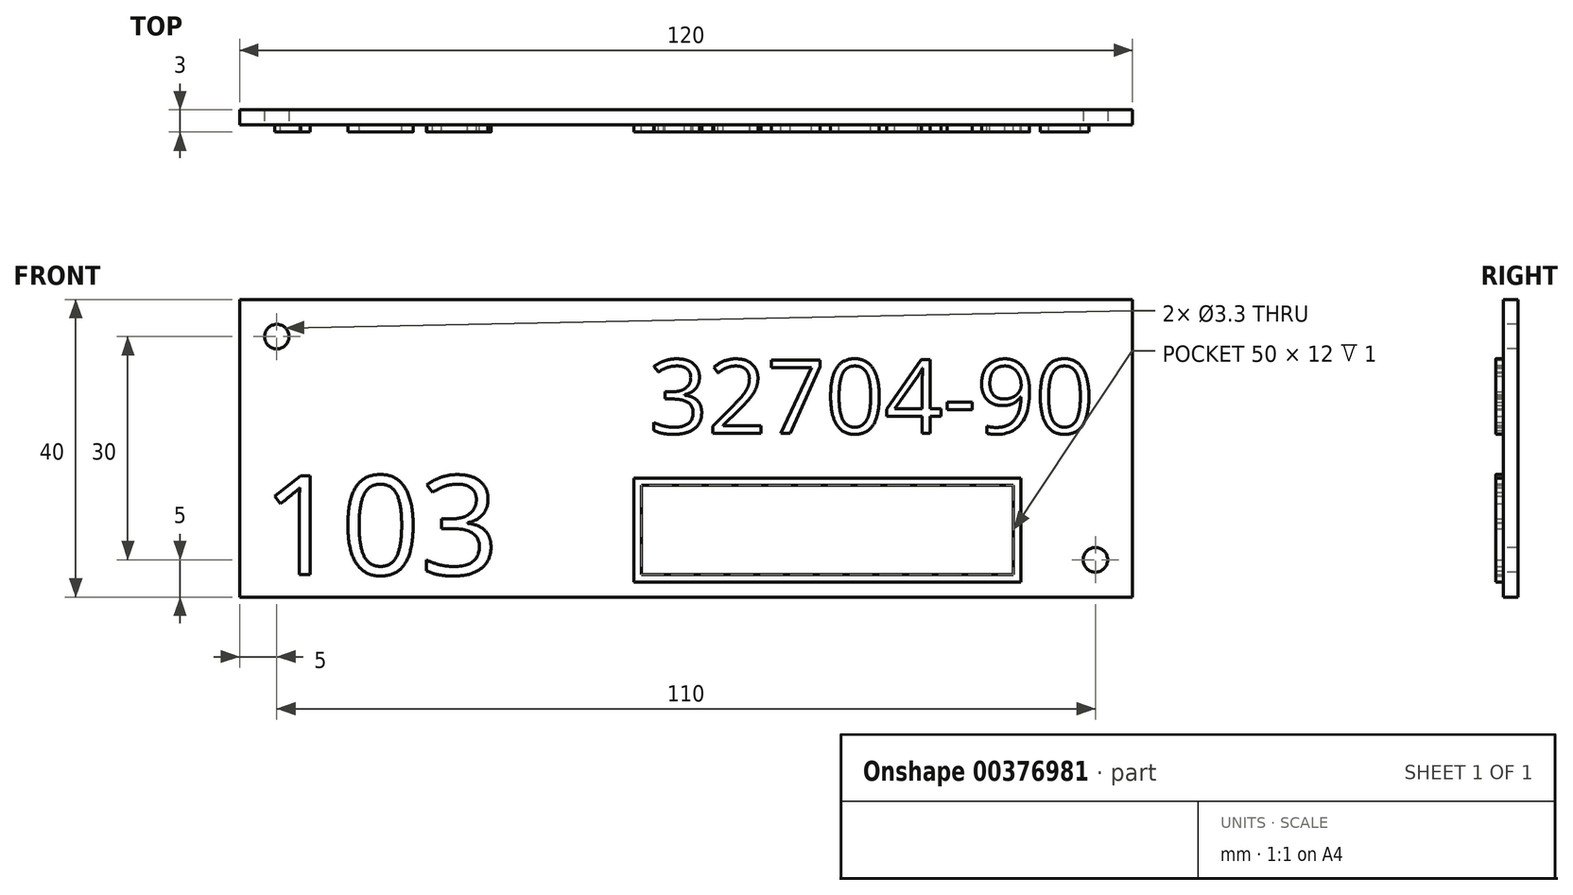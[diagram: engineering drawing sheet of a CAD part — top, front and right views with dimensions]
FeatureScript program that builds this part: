
annotation { "Feature Type Name" : "Feature", "Feature Type Description" : "" }
export const myFeature = defineFeature(function(context is Context, id is Id, definition is map)
    precondition{}
    {
        {
            var Q0;
            Q0=qCreatedBy(makeId("Front.planeOp"),FACE);
            var sketch = newSketch(context, id + "F0", { "sketchPlane" : qUnion([Q0])});
            skLineSegment(sketch, "E0.bottom", {"start": v(60, -20) * mm, "end": v(-60, -20) * mm});
            skLineSegment(sketch, "E0.top", {"start": v(60, 20) * mm, "end": v(-60, 20) * mm});
            skLineSegment(sketch, "E0.left", {"start": v(60, -20) * mm, "end": v(60, 20) * mm});
            skLineSegment(sketch, "E0.right", {"start": v(-60, -20) * mm, "end": v(-60, 20) * mm});
            skPoint(sketch, "E0.middle", {"position": v(0, 0) * mm});
            skSolve(sketch);
        }
        {
            var Q0;
            Q0=makeQuery(id+"F0.imprint","IMPRINT",FACE,{"disambiguationData":[TD([[makeQuery(id+"F0.imprint","IMPRINT",EDGE,{"derivedFrom":sQuery(id+"F0.wireOp",EDGE,"E0.bottom")}),-1.0]])]});
            extrude(context, id + "F1", {"entities" : qUnion([Q0]), "depth" : 2 * mm});
        }
        {
            var Q0;
            Q0=makeQuery(id+"F1.opExtrude","CAP_FACE",FACE,{"disambiguationData":[OSD([sQuery(id+"F0.wireOp",EDGE,"E0.bottom"),sQuery(id+"F0.wireOp",EDGE,"E0.top"),sQuery(id+"F0.wireOp",EDGE,"E0.left"),sQuery(id+"F0.wireOp",EDGE,"E0.right")])],"isStart":false});
            var sketch = newSketch(context, id + "F2", { "sketchPlane" : qUnion([Q0])});
            skPoint(sketch, "E1", {"position": v(-55, 15) * mm});
            skPoint(sketch, "E2", {"position": v(55, -15) * mm});
            skSolve(sketch);
        }
        {
            var Q0;
            Q0=sQuery(id+"F2.wireOp",VERTEX,"E1");
            var Q1;
            Q1=sQuery(id+"F2.wireOp",VERTEX,"E2");
            var Q2;
            Q2=makeQuery(id+"F1.opExtrude","SWEPT_BODY",BODY,{"disambiguationData":[OSD([sQuery(id+"F0.wireOp",EDGE,"E0.bottom"),sQuery(id+"F0.wireOp",EDGE,"E0.top"),sQuery(id+"F0.wireOp",EDGE,"E0.left"),sQuery(id+"F0.wireOp",EDGE,"E0.right")])]});
            hole(context, id + "F3", {"style" : HoleStyle.SIMPLE, "endStyle" : HoleEndStyle.THROUGH, "holeDiameter" : 3.3 * mm, "locations" : qUnion([Q0, Q1]), "scope" : qUnion([Q2]), "isTappedThrough" : true});
        }
        {
            var Q0;
            Q0=makeQuery(id+"F1.opExtrude","CAP_FACE",FACE,{"disambiguationData":[OSD([sQuery(id+"F0.wireOp",EDGE,"E0.bottom"),sQuery(id+"F0.wireOp",EDGE,"E0.top"),sQuery(id+"F0.wireOp",EDGE,"E0.left"),sQuery(id+"F0.wireOp",EDGE,"E0.right")])],"isStart":false});
            var sketch = newSketch(context, id + "F4", { "sketchPlane" : qUnion([Q0])});
            skText(sketch, "E3", { "text": "32704-90", "fontName": "OpenSans-Regular.ttf"});
            const initialGuessF4  = {"E3": [-0.005, 0.002, 1, 0, 0.00996]};
            skSetInitialGuess(sketch, initialGuessF4);
            skSolve(sketch);
        }
        {
            var Q0;
            Q0=qSketchRegion(id+"F4",true);
            extrude(context, id + "F5", {"entities" : qUnion([Q0]), "operationType" : NewBodyOperationType.ADD, "depth" : 1 * mm});
        }
        {
            var Q0;
            {var subQ0=sQuery(id+"F0.wireOp",EDGE,"E0.top");var subQ1=sQuery(id+"F0.wireOp",EDGE,"E0.left");var subQ2=sQuery(id+"F0.wireOp",EDGE,"E0.right");var subQ3=sQuery(id+"F0.wireOp",EDGE,"E0.bottom");Q0=makeQuery(id+"F5.boolean.opBoolean","SPLIT",FACE,{"disambiguationData":[TD([makeQuery(id+"F1.opExtrude","SWEPT_FACE",FACE,{"disambiguationData":[OSD([subQ3])]})])],"derivedFrom":makeQuery(id+"F1.opExtrude","CAP_FACE",FACE,{"disambiguationData":[OSD([subQ3,subQ0,subQ1,subQ2])],"isStart":false})});}
            var sketch = newSketch(context, id + "F6", { "sketchPlane" : qUnion([Q0])});
            skText(sketch, "E4", { "text": "103", "fontName": "OpenSans-Regular.ttf"});
            const initialGuessF6  = {"E4": [-0.057, -0.017, 1, 0, 0.01338]};
            skSetInitialGuess(sketch, initialGuessF6);
            skSolve(sketch);
        }
        {
            var Q0;
            Q0=qSketchRegion(id+"F6",true);
            extrude(context, id + "F7", {"entities" : qUnion([Q0]), "operationType" : NewBodyOperationType.ADD, "depth" : 1 * mm});
        }
        {
            var Q0;
            {var subQ46=sQuery(id+"F0.wireOp",EDGE,"E0.top");var subQ48=sQuery(id+"F0.wireOp",EDGE,"E0.left");var subQ66=sQuery(id+"F0.wireOp",EDGE,"E0.right");var subQ76=sQuery(id+"F0.wireOp",EDGE,"E0.bottom");var subQ77=makeQuery(id+"F1.opExtrude","SWEPT_FACE",FACE,{"disambiguationData":[OSD([subQ76])]});Q0=makeQuery(id+"F7.boolean.opBoolean","SPLIT",FACE,{"disambiguationData":[TD([subQ77])],"derivedFrom":makeQuery(id+"F5.boolean.opBoolean","SPLIT",FACE,{"disambiguationData":[TD([subQ77])],"derivedFrom":makeQuery(id+"F1.opExtrude","CAP_FACE",FACE,{"disambiguationData":[OSD([subQ76,subQ46,subQ48,subQ66])],"isStart":false})})});}
            var sketch = newSketch(context, id + "F8", { "sketchPlane" : qUnion([Q0])});
            skLineSegment(sketch, "E5.bottom", {"start": v(45, -18) * mm, "end": v(-7, -18) * mm});
            skLineSegment(sketch, "E5.top", {"start": v(45, -4) * mm, "end": v(-7, -4) * mm});
            skLineSegment(sketch, "E5.left", {"start": v(45, -18) * mm, "end": v(45, -4) * mm});
            skLineSegment(sketch, "E5.right", {"start": v(-7, -18) * mm, "end": v(-7, -4) * mm});
            skPoint(sketch, "E5.middle", {"position": v(19, -11) * mm});
            skLineSegment(sketch, "E6.0", {"start": v(44, -5) * mm, "end": v(-6, -5) * mm});
            skLineSegment(sketch, "E6.1", {"start": v(44, -17) * mm, "end": v(44, -5) * mm});
            skLineSegment(sketch, "E6.2", {"start": v(44, -17) * mm, "end": v(-6, -17) * mm});
            skLineSegment(sketch, "E6.3", {"start": v(-6, -17) * mm, "end": v(-6, -5) * mm});
            skSolve(sketch);
        }
        {
            var Q0;
            Q0=makeQuery(id+"F8.imprint","IMPRINT",FACE,{"disambiguationData":[TD([[makeQuery(id+"F8.imprint","IMPRINT",EDGE,{"derivedFrom":sQuery(id+"F8.wireOp",EDGE,"E5.bottom")}),-1.0]])]});
            extrude(context, id + "F9", {"entities" : qUnion([Q0]), "operationType" : NewBodyOperationType.ADD, "depth" : 1 * mm});
        }
    });
